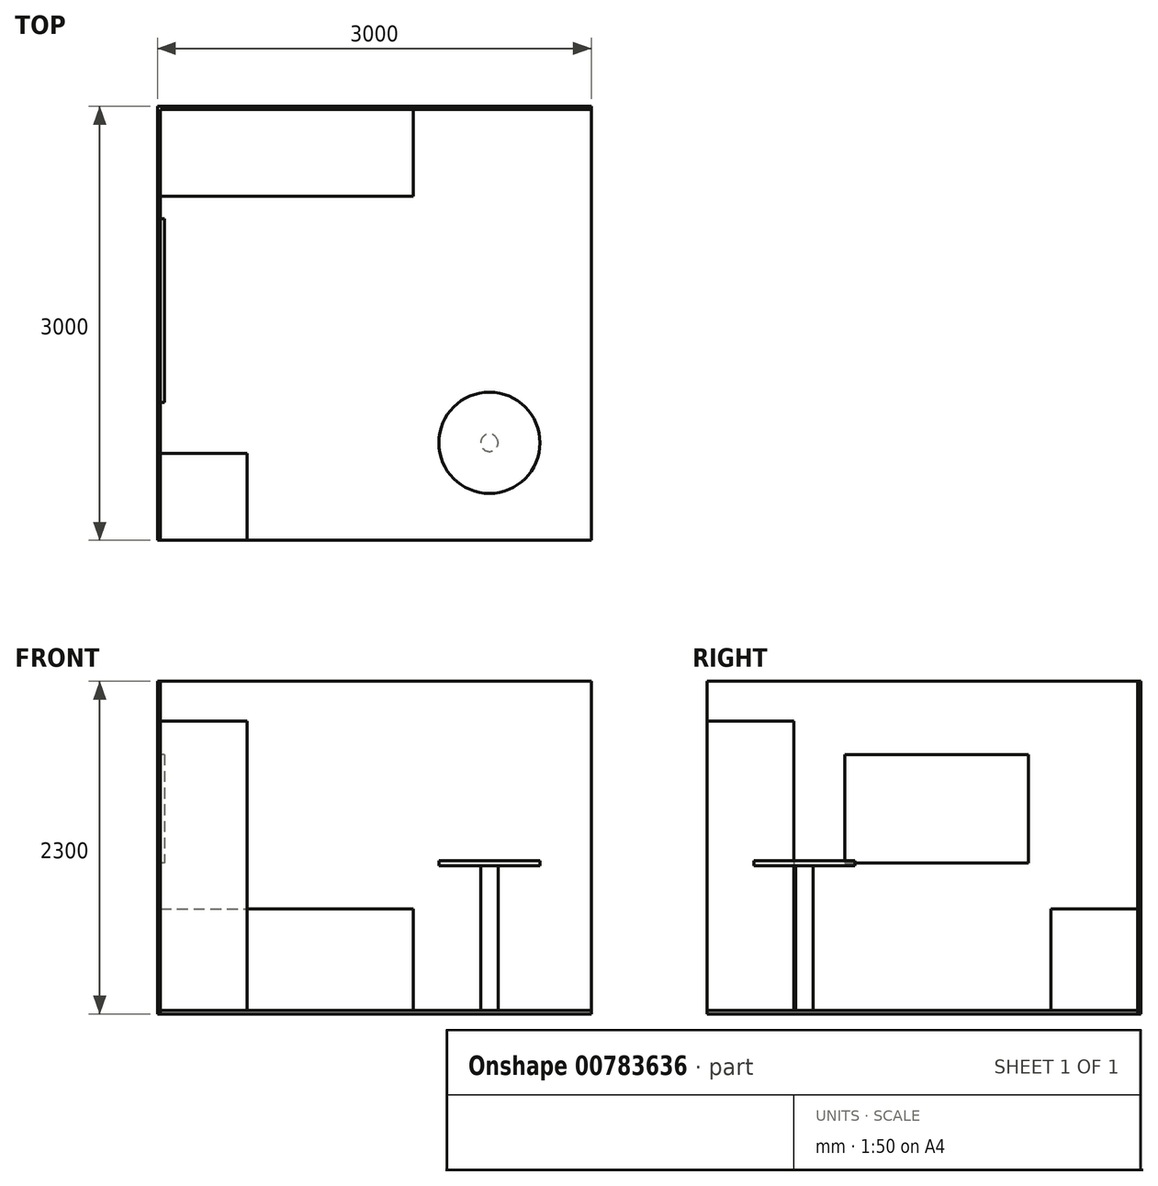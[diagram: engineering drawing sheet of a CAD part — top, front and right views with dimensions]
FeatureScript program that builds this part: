
annotation { "Feature Type Name" : "Feature", "Feature Type Description" : "" }
export const myFeature = defineFeature(function(context is Context, id is Id, definition is map)
    precondition{}
    {
        {
            var Q0;
            Q0=qCreatedBy(makeId("Top.planeOp"),FACE);
            var sketch = newSketch(context, id + "F0", { "sketchPlane" : qUnion([Q0])});
            skLineSegment(sketch, "E0.bottom", {"start": v(0, 0) * mm, "end": v(-3000, 0) * mm});
            skLineSegment(sketch, "E0.top", {"start": v(0, 3000) * mm, "end": v(-3000, 3000) * mm});
            skLineSegment(sketch, "E0.left", {"start": v(0, 0) * mm, "end": v(0, 3000) * mm});
            skLineSegment(sketch, "E0.right", {"start": v(-3000, 0) * mm, "end": v(-3000, 3000) * mm});
            skSolve(sketch);
        }
        {
            var Q0;
            Q0=qCreatedBy(makeId("Top.planeOp"),FACE);
            var sketch = newSketch(context, id + "F1", { "sketchPlane" : qUnion([Q0])});
            skLineSegment(sketch, "E1", {"start": v(0, 3000) * mm, "end": v(-3000, 3000) * mm});
            skLineSegment(sketch, "E2", {"start": v(-3000, 3000) * mm, "end": v(-3000, 0) * mm});
            skLineSegment(sketch, "E3", {"start": v(-2980, 0) * mm, "end": v(-3000, 0) * mm});
            skLineSegment(sketch, "E4", {"start": v(-2980, 0) * mm, "end": v(-2980, 2980) * mm});
            skLineSegment(sketch, "E5", {"start": v(-2980, 2980) * mm, "end": v(0, 2980) * mm});
            skLineSegment(sketch, "E6", {"start": v(0, 3000) * mm, "end": v(0, 2980) * mm});
            skSolve(sketch);
        }
        {
            var Q0;
            Q0 = qSketchRegion(id + "F0", true);
            extrude(context, id + "F2", {"entities" : qUnion([Q0]), "depth" : 25 * mm, "offsetDistance" : 25 * mm});
        }
        {
            var Q0;
            Q0 = qSketchRegion(id + "F1", true);
            extrude(context, id + "F3", {"entities" : qUnion([Q0]), "depth" : 2300 * mm, "offsetDistance" : 25 * mm});
        }
        {
            var Q0;
            Q0=makeQuery(id+"F2.opExtrude","CAP_FACE",FACE,{"disambiguationData":[OSD([sQuery(id+"F0.wireOp",EDGE,"E0.bottom"),sQuery(id+"F0.wireOp",EDGE,"E0.top"),sQuery(id+"F0.wireOp",EDGE,"E0.left"),sQuery(id+"F0.wireOp",EDGE,"E0.right")])],"isStart":false});
            var sketch = newSketch(context, id + "F4", { "sketchPlane" : qUnion([Q0])});
            skLineSegment(sketch, "E7.bottom", {"start": v(-2980, 2980) * mm, "end": v(-1230, 2980) * mm});
            skLineSegment(sketch, "E7.top", {"start": v(-2980, 2380) * mm, "end": v(-1230, 2380) * mm});
            skLineSegment(sketch, "E7.left", {"start": v(-2980, 2980) * mm, "end": v(-2980, 2380) * mm});
            skLineSegment(sketch, "E7.right", {"start": v(-1230, 2980) * mm, "end": v(-1230, 2380) * mm});
            skSolve(sketch);
        }
        {
            var Q0;
            Q0 = qSketchRegion(id + "F4", true);
            extrude(context, id + "F5", {"entities" : qUnion([Q0]), "depth" : 700 * mm, "offsetDistance" : 25 * mm});
        }
        {
            var Q0;
            Q0=makeQuery(id+"F2.opExtrude","CAP_FACE",FACE,{"disambiguationData":[OSD([sQuery(id+"F0.wireOp",EDGE,"E0.bottom"),sQuery(id+"F0.wireOp",EDGE,"E0.top"),sQuery(id+"F0.wireOp",EDGE,"E0.left"),sQuery(id+"F0.wireOp",EDGE,"E0.right")])],"isStart":false});
            var sketch = newSketch(context, id + "F6", { "sketchPlane" : qUnion([Q0])});
            skLineSegment(sketch, "E8.bottom", {"start": v(-2979.3, 0) * mm, "end": v(-2379.3, 0) * mm});
            skLineSegment(sketch, "E8.top", {"start": v(-2979.3, 600) * mm, "end": v(-2379.3, 600) * mm});
            skLineSegment(sketch, "E8.left", {"start": v(-2979.3, 0) * mm, "end": v(-2979.3, 600) * mm});
            skLineSegment(sketch, "E8.right", {"start": v(-2379.3, 0) * mm, "end": v(-2379.3, 600) * mm});
            skSolve(sketch);
        }
        {
            var Q0;
            Q0 = qSketchRegion(id + "F6", true);
            extrude(context, id + "F7", {"entities" : qUnion([Q0]), "depth" : 2000 * mm, "offsetDistance" : 25 * mm});
        }
        {
            var Q0;
            Q0=makeQuery(id+"F2.opExtrude","CAP_FACE",FACE,{"disambiguationData":[OSD([sQuery(id+"F0.wireOp",EDGE,"E0.bottom"),sQuery(id+"F0.wireOp",EDGE,"E0.top"),sQuery(id+"F0.wireOp",EDGE,"E0.left"),sQuery(id+"F0.wireOp",EDGE,"E0.right")])],"isStart":false});
            var sketch = newSketch(context, id + "F8", { "sketchPlane" : qUnion([Q0])});
            skLineSegment(sketch, "E9", {"start": v(-2423.38, 2070.16) * mm, "end": v(-2923.13, 1888.27) * mm});
            skLineSegment(sketch, "E10", {"start": v(-2923.13, 1888.27) * mm, "end": v(-2923.13, 1332.4) * mm});
            skLineSegment(sketch, "E11", {"start": v(-2923.13, 1332.4) * mm, "end": v(-2423.38, 1150.51) * mm});
            skSolve(sketch);
        }
        {
            var Q0;
            Q0=makeQuery(id+"F8.imprint","IMPRINT",FACE,{"disambiguationData":[TD([[makeQuery(id+"F8.imprint","IMPRINT",EDGE,{"derivedFrom":makeQuery(id+"F2.opExtrude","CAP_EDGE",EDGE,{"disambiguationData":[OSD([sQuery(id+"F0.wireOp",EDGE,"E0.bottom")])],"isStart":false})}),-1.0]])]});
            var sketch = newSketch(context, id + "F9", { "sketchPlane" : qUnion([Q0])});
            skCircle(sketch, "E12", {"center": v(-704.34, 673.72) * mm, "radius": 60 * mm});
            skSolve(sketch);
        }
        {
            var Q0;
            Q0 = qSketchRegion(id + "F9", true);
            extrude(context, id + "F10", {"entities" : qUnion([Q0]), "depth" : 1000 * mm, "offsetDistance" : 25 * mm});
        }
        {
            var Q0;
            Q0=makeQuery(id+"F10.opExtrude","CAP_FACE",FACE,{"disambiguationData":[OSD([sQuery(id+"F9.wireOp",EDGE,"E12")])],"isStart":false});
            var sketch = newSketch(context, id + "F11", { "sketchPlane" : qUnion([Q0])});
            skCircle(sketch, "E13", {"center": v(-704.34, 673.72) * mm, "radius": 350 * mm});
            skSolve(sketch);
        }
        {
            var Q0;
            Q0 = qSketchRegion(id + "F11", true);
            extrude(context, id + "F12", {"entities" : qUnion([Q0]), "operationType" : NewBodyOperationType.ADD, "depth" : 35 * mm, "offsetDistance" : 25 * mm});
        }
        {
            var Q0;
            Q0=makeQuery(id+"F3.opExtrude","SWEPT_FACE",FACE,{"disambiguationData":[OSD([sQuery(id+"F1.wireOp",EDGE,"E4")])]});
            var sketch = newSketch(context, id + "F13", { "sketchPlane" : qUnion([Q0])});
            skLineSegment(sketch, "E14.bottom", {"start": v(952.83, 1793.8) * mm, "end": v(2222.83, 1793.8) * mm});
            skLineSegment(sketch, "E14.top", {"start": v(952.83, 1043.8) * mm, "end": v(2222.83, 1043.8) * mm});
            skLineSegment(sketch, "E14.left", {"start": v(952.83, 1793.8) * mm, "end": v(952.83, 1043.8) * mm});
            skLineSegment(sketch, "E14.right", {"start": v(2222.83, 1793.8) * mm, "end": v(2222.83, 1043.8) * mm});
            skSolve(sketch);
        }
        {
            var Q0;
            Q0 = qSketchRegion(id + "F13", true);
            extrude(context, id + "F14", {"entities" : qUnion([Q0]), "depth" : 30 * mm, "offsetDistance" : 25 * mm});
        }
    });
